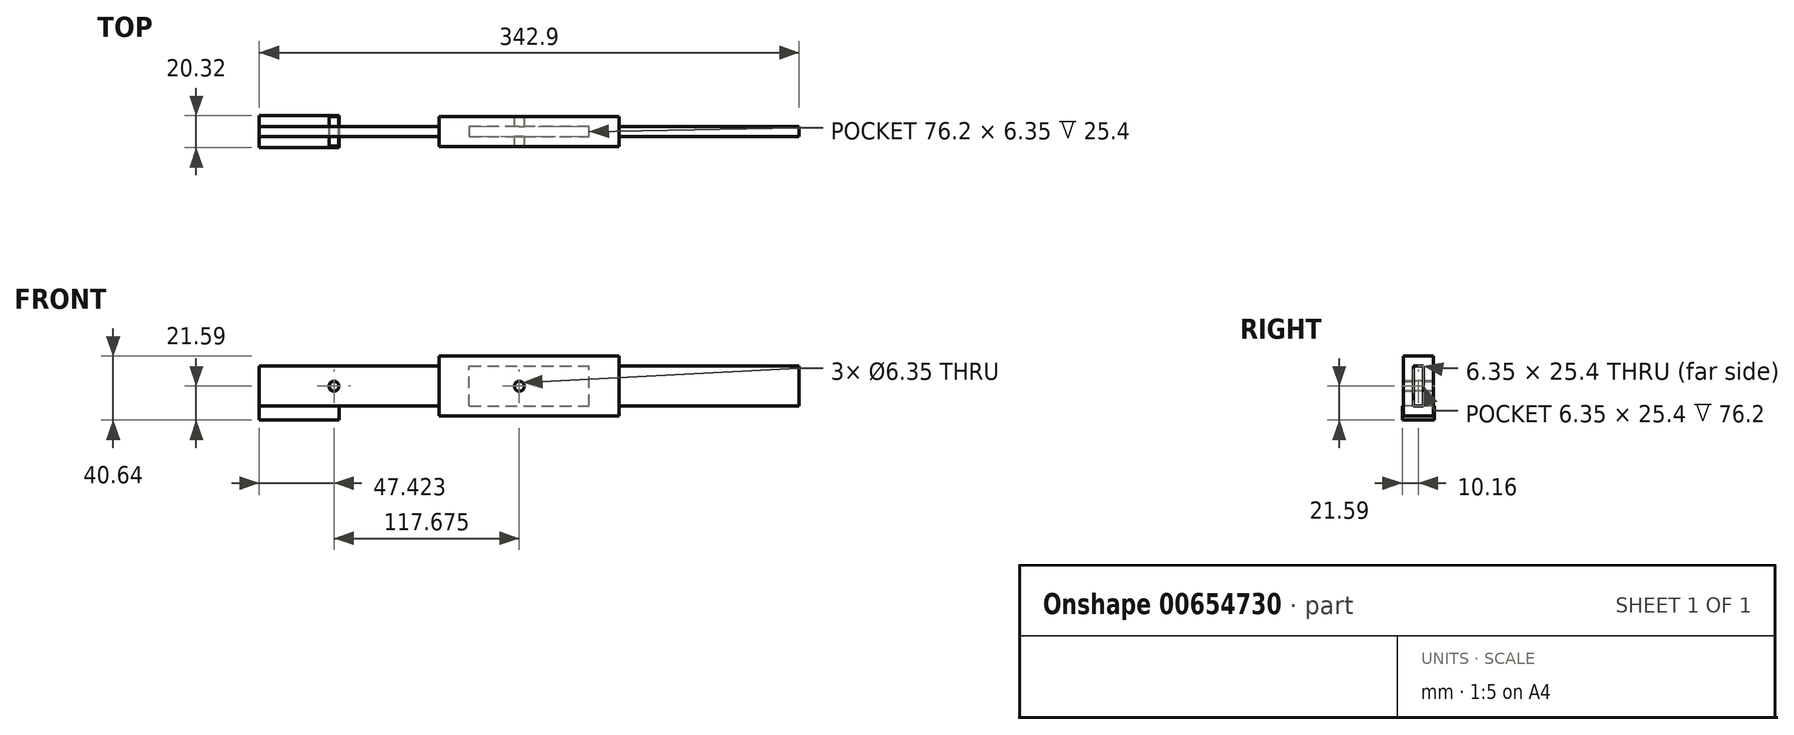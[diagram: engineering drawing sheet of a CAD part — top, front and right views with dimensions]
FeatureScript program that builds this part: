
annotation { "Feature Type Name" : "Feature", "Feature Type Description" : "" }
export const myFeature = defineFeature(function(context is Context, id is Id, definition is map)
    precondition{}
    {
        {
            var Q0;
            Q0=qCreatedBy(makeId("Top.planeOp"),FACE);
            var sketch = newSketch(context, id + "F0", { "sketchPlane" : qUnion([Q0])});
            skLineSegment(sketch, "E0", {"start": v(-60.37, 0) * mm, "end": v(-60.37, 3.18) * mm});
            skLineSegment(sketch, "E1", {"start": v(-60.37, 0) * mm, "end": v(-60.37, -3.18) * mm});
            skLineSegment(sketch, "E2", {"start": v(-60.37, -3.18) * mm, "end": v(53.93, -3.17) * mm});
            skLineSegment(sketch, "E3", {"start": v(53.93, -3.17) * mm, "end": v(53.93, -9.52) * mm});
            skLineSegment(sketch, "E4", {"start": v(53.93, -9.52) * mm, "end": v(168.23, -9.52) * mm});
            skLineSegment(sketch, "E5", {"start": v(168.23, -9.52) * mm, "end": v(168.23, -3.17) * mm});
            skLineSegment(sketch, "E6", {"start": v(168.23, -3.17) * mm, "end": v(282.53, -3.17) * mm});
            skLineSegment(sketch, "E7", {"start": v(282.53, -3.17) * mm, "end": v(282.53, 3.18) * mm});
            skLineSegment(sketch, "E8", {"start": v(282.53, 3.18) * mm, "end": v(168.23, 3.18) * mm});
            skLineSegment(sketch, "E9", {"start": v(168.23, 3.18) * mm, "end": v(168.23, 9.53) * mm});
            skLineSegment(sketch, "E10", {"start": v(168.23, 9.53) * mm, "end": v(53.93, 9.53) * mm});
            skLineSegment(sketch, "E11", {"start": v(53.93, 9.53) * mm, "end": v(53.93, 3.18) * mm});
            skLineSegment(sketch, "E12", {"start": v(53.93, 3.18) * mm, "end": v(-60.37, 3.18) * mm});
            skSolve(sketch);
        }
        {
            var Q0;
            Q0=makeQuery(id+"F0.imprint","IMPRINT",FACE,{"disambiguationData":[TD([[makeQuery(id+"F0.imprint","IMPRINT",EDGE,{"derivedFrom":sQuery(id+"F0.wireOp",EDGE,"E0")}),-1.0]])]});
            extrude(context, id + "F1", {"entities" : qUnion([Q0]), "depth" : 25.4 * mm, "offsetDistance" : 25.4 * mm});
        }
        {
            var Q0;
            Q0=makeQuery(id+"F1.opExtrude","CAP_FACE",FACE,{"disambiguationData":[OSD([sQuery(id+"F0.wireOp",EDGE,"E0"),sQuery(id+"F0.wireOp",EDGE,"E1"),sQuery(id+"F0.wireOp",EDGE,"E2"),sQuery(id+"F0.wireOp",EDGE,"E3"),sQuery(id+"F0.wireOp",EDGE,"E4"),sQuery(id+"F0.wireOp",EDGE,"E5"),sQuery(id+"F0.wireOp",EDGE,"E6"),sQuery(id+"F0.wireOp",EDGE,"E7"),sQuery(id+"F0.wireOp",EDGE,"E8"),sQuery(id+"F0.wireOp",EDGE,"E9"),sQuery(id+"F0.wireOp",EDGE,"E10"),sQuery(id+"F0.wireOp",EDGE,"E11"),sQuery(id+"F0.wireOp",EDGE,"E12")])],"isStart":false});
            var sketch = newSketch(context, id + "F2", { "sketchPlane" : qUnion([Q0])});
            skLineSegment(sketch, "E13", {"start": v(72.98, -3.17) * mm, "end": v(149.18, -3.17) * mm});
            skLineSegment(sketch, "E14", {"start": v(149.18, -3.17) * mm, "end": v(149.18, 3.18) * mm});
            skLineSegment(sketch, "E15", {"start": v(149.18, 3.18) * mm, "end": v(72.98, 3.18) * mm});
            skLineSegment(sketch, "E16", {"start": v(72.98, 3.18) * mm, "end": v(72.98, -3.17) * mm});
            skSolve(sketch);
        }
        {
            var Q0;
            Q0=makeQuery(id+"F2.imprint","IMPRINT",FACE,{"disambiguationData":[TD([[makeQuery(id+"F2.imprint","IMPRINT",EDGE,{"derivedFrom":sQuery(id+"F2.wireOp",EDGE,"E13")}),1.0]])]});
            extrude(context, id + "F3", {"entities" : qUnion([Q0]), "operationType" : NewBodyOperationType.REMOVE, "oppositeDirection" : true, "depth" : 25.4 * mm, "offsetDistance" : 25.4 * mm});
        }
        {
            var Q0;
            Q0=makeQuery(id+"F1.opExtrude","SWEPT_FACE",FACE,{"disambiguationData":[OSD([sQuery(id+"F0.wireOp",EDGE,"E4")])]});
            var sketch = newSketch(context, id + "F4", { "sketchPlane" : qUnion([Q0])});
            skLineSegment(sketch, "E17", {"start": v(53.93, 12.7) * mm, "end": v(104.73, 12.7) * mm});
            skCircle(sketch, "E18", {"center": v(104.73, 12.7) * mm, "radius": 3.18 * mm});
            skSolve(sketch);
        }
        {
            var Q0;
            Q0=makeQuery(id+"F4.imprint","IMPRINT",FACE,{"disambiguationData":[TD([[makeQuery(id+"F4.imprint","IMPRINT",EDGE,{"derivedFrom":sQuery(id+"F4.wireOp",EDGE,"E18")}),1.0]])]});
            extrude(context, id + "F5", {"entities" : qUnion([Q0]), "operationType" : NewBodyOperationType.REMOVE, "oppositeDirection" : true, "depth" : 25.4 * mm, "offsetDistance" : 25.4 * mm});
        }
        {
            var Q0;
            Q0=makeQuery(id+"F1.opExtrude","CAP_FACE",FACE,{"disambiguationData":[OSD([sQuery(id+"F0.wireOp",EDGE,"E0"),sQuery(id+"F0.wireOp",EDGE,"E1"),sQuery(id+"F0.wireOp",EDGE,"E2"),sQuery(id+"F0.wireOp",EDGE,"E3"),sQuery(id+"F0.wireOp",EDGE,"E4"),sQuery(id+"F0.wireOp",EDGE,"E5"),sQuery(id+"F0.wireOp",EDGE,"E6"),sQuery(id+"F0.wireOp",EDGE,"E7"),sQuery(id+"F0.wireOp",EDGE,"E8"),sQuery(id+"F0.wireOp",EDGE,"E9"),sQuery(id+"F0.wireOp",EDGE,"E10"),sQuery(id+"F0.wireOp",EDGE,"E11"),sQuery(id+"F0.wireOp",EDGE,"E12")])],"isStart":false});
            var sketch = newSketch(context, id + "F6", { "sketchPlane" : qUnion([Q0])});
            skLineSegment(sketch, "E19.bottom", {"start": v(53.93, -9.52) * mm, "end": v(168.23, -9.52) * mm});
            skLineSegment(sketch, "E19.top", {"start": v(53.93, 9.53) * mm, "end": v(168.23, 9.53) * mm});
            skLineSegment(sketch, "E19.left", {"start": v(53.93, -9.52) * mm, "end": v(53.93, 9.53) * mm});
            skLineSegment(sketch, "E19.right", {"start": v(168.23, -9.52) * mm, "end": v(168.23, 9.53) * mm});
            skSolve(sketch);
        }
        {
            var Q0;
            Q0 = qSketchRegion(id + "F6", true);
            extrude(context, id + "F7", {"entities" : qUnion([Q0]), "operationType" : NewBodyOperationType.ADD, "depth" : 6.35 * mm, "offsetDistance" : 25.4 * mm});
        }
        {
            var Q0;
            Q0=makeQuery(id+"F1.opExtrude","CAP_FACE",FACE,{"disambiguationData":[OSD([sQuery(id+"F0.wireOp",EDGE,"E0"),sQuery(id+"F0.wireOp",EDGE,"E1"),sQuery(id+"F0.wireOp",EDGE,"E2"),sQuery(id+"F0.wireOp",EDGE,"E3"),sQuery(id+"F0.wireOp",EDGE,"E4"),sQuery(id+"F0.wireOp",EDGE,"E5"),sQuery(id+"F0.wireOp",EDGE,"E6"),sQuery(id+"F0.wireOp",EDGE,"E7"),sQuery(id+"F0.wireOp",EDGE,"E8"),sQuery(id+"F0.wireOp",EDGE,"E9"),sQuery(id+"F0.wireOp",EDGE,"E10"),sQuery(id+"F0.wireOp",EDGE,"E11"),sQuery(id+"F0.wireOp",EDGE,"E12")])],"isStart":true});
            var sketch = newSketch(context, id + "F8", { "sketchPlane" : qUnion([Q0])});
            skLineSegment(sketch, "E20.bottom", {"start": v(53.93, -9.53) * mm, "end": v(168.23, -9.53) * mm});
            skLineSegment(sketch, "E20.top", {"start": v(53.93, 9.52) * mm, "end": v(168.23, 9.52) * mm});
            skLineSegment(sketch, "E20.left", {"start": v(53.93, -9.53) * mm, "end": v(53.93, 9.52) * mm});
            skLineSegment(sketch, "E20.right", {"start": v(168.23, -9.53) * mm, "end": v(168.23, 9.52) * mm});
            skSolve(sketch);
        }
        {
            var Q0;
            Q0 = qSketchRegion(id + "F8", true);
            extrude(context, id + "F9", {"entities" : qUnion([Q0]), "operationType" : NewBodyOperationType.ADD, "depth" : 6.35 * mm, "offsetDistance" : 25.4 * mm});
        }
        {
            var Q0;
            Q0=makeQuery(id+"F1.opExtrude","SWEPT_FACE",FACE,{"disambiguationData":[OSD([sQuery(id+"F0.wireOp",EDGE,"E2")])]});
            var sketch = newSketch(context, id + "F10", { "sketchPlane" : qUnion([Q0])});
            skPoint(sketch, "E21.center.orphan", {"position": v(0, 12.7) * mm});
            skPoint(sketch, "E22.orphan", {"position": v(0, 25.4) * mm});
            skPoint(sketch, "E23.start.orphan", {"position": v(0, 0) * mm});
            skLineSegment(sketch, "E24", {"start": v(-60.37, 0) * mm, "end": v(-9.57, 0) * mm, "construction": true});
            skLineSegment(sketch, "E25", {"start": v(-12.95, 0) * mm, "end": v(-12.95, 25.4) * mm, "construction": true});
            skCircle(sketch, "E26", {"center": v(-12.95, 12.7) * mm, "radius": 3.18 * mm});
            skSolve(sketch);
        }
        {
            var Q0;
            Q0=makeQuery(id+"F10.imprint","IMPRINT",FACE,{"disambiguationData":[TD([[makeQuery(id+"F10.imprint","IMPRINT",EDGE,{"derivedFrom":sQuery(id+"F10.wireOp",EDGE,"E26")}),1.0]])]});
            extrude(context, id + "F11", {"entities" : qUnion([Q0]), "operationType" : NewBodyOperationType.REMOVE, "oppositeDirection" : true, "depth" : 25.4 * mm, "offsetDistance" : 25.4 * mm});
        }
        {
            var Q0;
            {var subQ0=sQuery(id+"F0.wireOp",EDGE,"E11");var subQ1=sQuery(id+"F0.wireOp",EDGE,"E3");var subQ2=sQuery(id+"F0.wireOp",EDGE,"E2");var subQ3=sQuery(id+"F0.wireOp",EDGE,"E1");var subQ4=sQuery(id+"F0.wireOp",EDGE,"E0");var subQ5=sQuery(id+"F0.wireOp",EDGE,"E12");Q0=makeQuery(id+"F9.boolean.opBoolean","SPLIT",FACE,{"disambiguationData":[TD([makeQuery(id+"F1.opExtrude","SWEPT_FACE",FACE,{"disambiguationData":[OSD([subQ2])]})])],"derivedFrom":makeQuery(id+"F1.opExtrude","CAP_FACE",FACE,{"disambiguationData":[OSD([subQ4,subQ3,subQ2,subQ1,sQuery(id+"F0.wireOp",EDGE,"E4"),sQuery(id+"F0.wireOp",EDGE,"E5"),sQuery(id+"F0.wireOp",EDGE,"E6"),sQuery(id+"F0.wireOp",EDGE,"E7"),sQuery(id+"F0.wireOp",EDGE,"E8"),sQuery(id+"F0.wireOp",EDGE,"E9"),sQuery(id+"F0.wireOp",EDGE,"E10"),subQ0,subQ5])],"isStart":true})});}
            var sketch = newSketch(context, id + "F12", { "sketchPlane" : qUnion([Q0])});
            skLineSegment(sketch, "E27", {"start": v(-60.37, 0) * mm, "end": v(-9.57, 0) * mm, "construction": true});
            skLineSegment(sketch, "E28.bottom", {"start": v(-60.37, 0) * mm, "end": v(-9.53, 0) * mm});
            skLineSegment(sketch, "E28.top", {"start": v(-60.37, 10.16) * mm, "end": v(-9.53, 10.16) * mm});
            skLineSegment(sketch, "E28.left", {"start": v(-60.37, 0) * mm, "end": v(-60.37, 10.16) * mm});
            skLineSegment(sketch, "E28.right", {"start": v(-9.53, 0) * mm, "end": v(-9.53, 10.16) * mm});
            skLineSegment(sketch, "E29.left", {"start": v(-60.37, 0) * mm, "end": v(-60.37, 0) * mm});
            skLineSegment(sketch, "E29.right", {"start": v(-9.53, 0) * mm, "end": v(-9.53, 0) * mm});
            skLineSegment(sketch, "E30.top", {"start": v(-60.37, -10.16) * mm, "end": v(-9.53, -10.16) * mm});
            skLineSegment(sketch, "E30.left", {"start": v(-60.37, 0) * mm, "end": v(-60.37, -10.16) * mm});
            skLineSegment(sketch, "E30.right", {"start": v(-9.53, 0) * mm, "end": v(-9.53, -10.16) * mm});
            skSolve(sketch);
        }
        {
            var Q0;
            Q0 = qSketchRegion(id + "F12", true);
            extrude(context, id + "F13", {"entities" : qUnion([Q0]), "operationType" : NewBodyOperationType.ADD, "depth" : 8.9 * mm, "offsetDistance" : 25.4 * mm});
        }
        {
            var Q0;
            Q0=makeQuery(id+"F9.boolean.opBoolean","MERGE",FACE,{"derivedFrom":[makeQuery(id+"F7.boolean.opBoolean","MERGE",FACE,{"derivedFrom":[makeQuery(id+"F1.opExtrude","SWEPT_FACE",FACE,{"disambiguationData":[OSD([sQuery(id+"F0.wireOp",EDGE,"E10")])]}),makeQuery(id+"F7.opExtrude","SWEPT_FACE",FACE,{"disambiguationData":[OSD([sQuery(id+"F6.wireOp",EDGE,"E19.top")])]})]}),makeQuery(id+"F9.opExtrude","SWEPT_FACE",FACE,{"disambiguationData":[OSD([sQuery(id+"F8.wireOp",EDGE,"E20.bottom")])]})]});
            var sketch = newSketch(context, id + "F14", { "sketchPlane" : qUnion([Q0])});
            skCircle(sketch, "E31", {"center": v(12.93, 12.64) * mm, "radius": 3.05 * mm});
            skSolve(sketch);
        }
        {
            var Q0;
            Q0=makeQuery(id+"F14.imprint","IMPRINT",FACE,{"disambiguationData":[TD([[makeQuery(id+"F14.imprint","IMPRINT",EDGE,{"derivedFrom":sQuery(id+"F14.wireOp",EDGE,"E31")}),1.0]])]});
            extrude(context, id + "F15", {"entities" : qUnion([Q0]), "oppositeDirection" : true, "depth" : 18.8 * mm, "offsetDistance" : 25.4 * mm});
        }
    });
